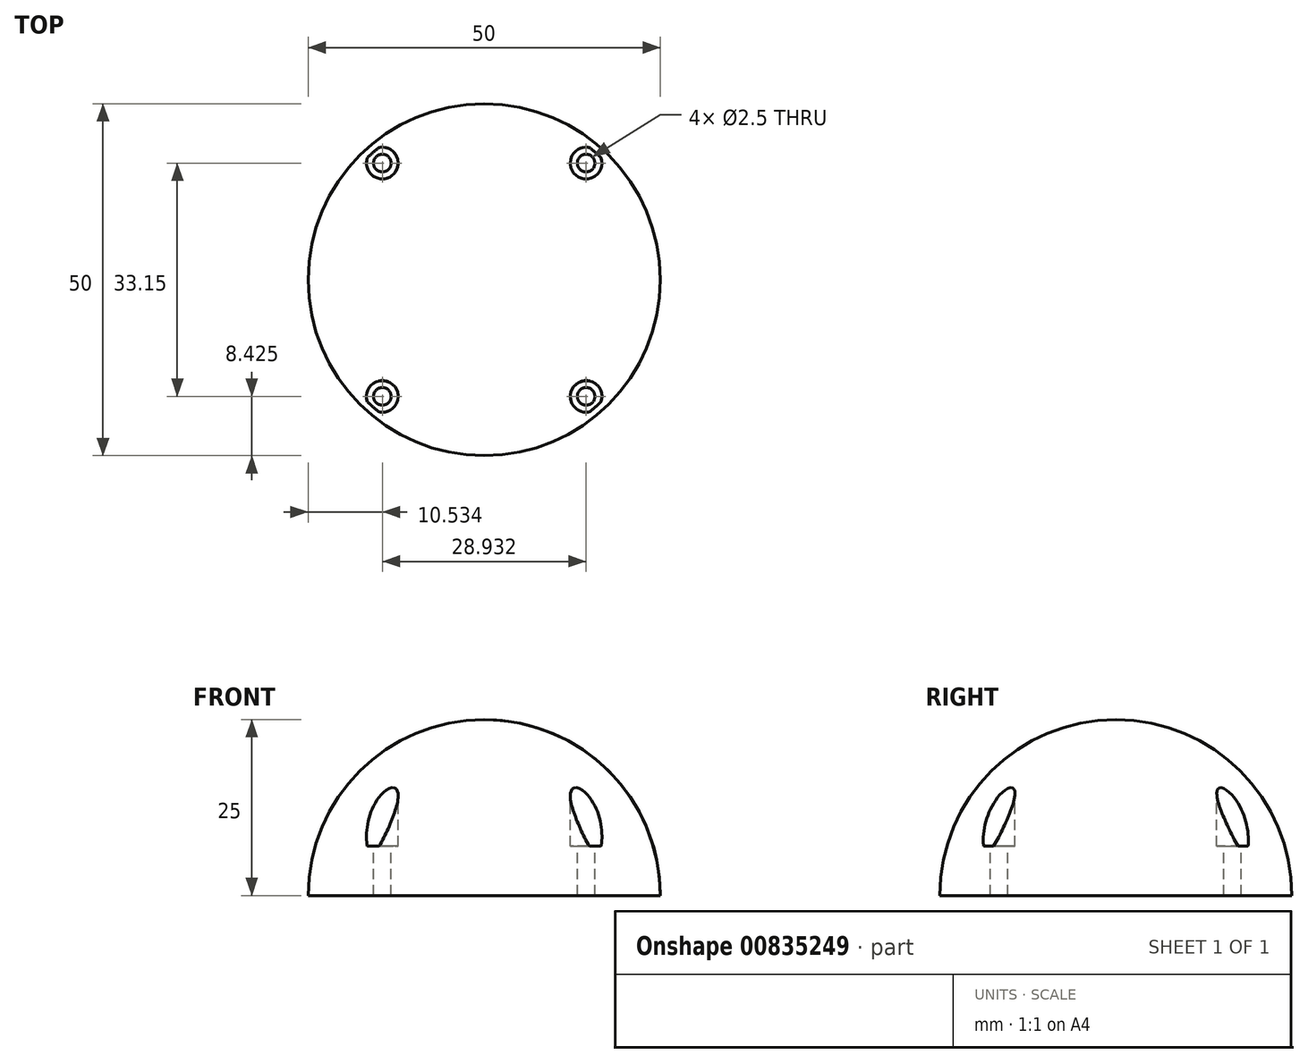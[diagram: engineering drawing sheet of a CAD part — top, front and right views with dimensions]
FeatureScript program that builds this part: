
annotation { "Feature Type Name" : "Feature", "Feature Type Description" : "" }
export const myFeature = defineFeature(function(context is Context, id is Id, definition is map)
    precondition{}
    {
        {
            var Q0;
            Q0=qCreatedBy(makeId("Top.planeOp"),FACE);
            var sketch = newSketch(context, id + "F0", { "sketchPlane" : qUnion([Q0])});
            skCircle(sketch, "E0", {"center": v(0, 0) * mm, "radius": 25 * mm});
            skSolve(sketch);
        }
        {
            var Q0;
            Q0=makeQuery(id+"F0.imprint","IMPRINT",FACE,{"disambiguationData":[TD([[makeQuery(id+"F0.imprint","IMPRINT",EDGE,{"derivedFrom":sQuery(id+"F0.wireOp",EDGE,"E0")}),1.0]])]});
            extrude(context, id + "F1", {"entities" : qUnion([Q0]), "depth" : 25 * mm, "offsetDistance" : 25 * mm});
        }
        {
            var Q0;
            Q0=makeQuery(id+"F1.opExtrude","CAP_FACE",FACE,{"disambiguationData":[OSD([sQuery(id+"F0.wireOp",EDGE,"E0")])],"isStart":false});
            var sketch = newSketch(context, id + "F2", { "sketchPlane" : qUnion([Q0])});
            skCircle(sketch, "E1", {"center": v(-14.47, -16.57) * mm, "radius": 3 * mm});
            skPoint(sketch, "E1.first.point", {"position": v(-16.44, -18.84) * mm});
            skPoint(sketch, "E1.second.point", {"position": v(-12.8, -14.08) * mm});
            skPoint(sketch, "E1.third.point", {"position": v(-15.23, -13.67) * mm});
            skCircle(sketch, "E2", {"center": v(-14.47, -16.57) * mm, "radius": 1.25 * mm});
            skCircle(sketch, "E3.MirrorC", {"center": v(-14.47, 16.57) * mm, "radius": 1.25 * mm});
            skCircle(sketch, "E4.MirrorC", {"center": v(-14.47, 16.57) * mm, "radius": 3 * mm});
            skCircle(sketch, "E5.MirrorC", {"center": v(14.47, -16.57) * mm, "radius": 1.25 * mm});
            skCircle(sketch, "E6.MirrorC", {"center": v(14.47, -16.57) * mm, "radius": 3 * mm});
            skCircle(sketch, "E7.MirrorC", {"center": v(14.47, 16.57) * mm, "radius": 3 * mm});
            skCircle(sketch, "E8.MirrorC", {"center": v(14.47, 16.57) * mm, "radius": 1.25 * mm});
            skSolve(sketch);
        }
        {
            var Q0;
            Q0=sQuery(id+"F2.wireOp",VERTEX,"E7.MirrorC.center");
            var Q1;
            Q1=sQuery(id+"F2.wireOp",VERTEX,"E5.MirrorC.center");
            var Q2;
            Q2=sQuery(id+"F2.wireOp",VERTEX,"E1.center");
            var Q3;
            Q3=sQuery(id+"F2.wireOp",VERTEX,"E3.MirrorC.center");
            var Q4;
            Q4=makeQuery(id+"F1.opExtrude","SWEPT_BODY",BODY,{"disambiguationData":[OSD([sQuery(id+"F0.wireOp",EDGE,"E0")])]});
            hole(context, id + "F3", {"style" : HoleStyle.C_BORE, "endStyle" : HoleEndStyle.THROUGH, "holeDiameter" : 2.5 * mm, "cBoreDiameter" : 4.5 * mm, "cBoreDepth" : 18 * mm, "majorDiameter" : 5 * mm, "isTappedThrough" : true, "tappedDepth" : 12 * mm, "tapClearance" : 3, "locations" : qUnion([Q0, Q1, Q2, Q3]), "scope" : qUnion([Q4])});
        }
        {
            var Q0;
            Q0=makeQuery(id+"F1.opExtrude","CAP_EDGE",EDGE,{"disambiguationData":[OSD([sQuery(id+"F0.wireOp",EDGE,"E0")])],"isStart":false});
            fillet(context, id + "F4", {"entities" : qUnion([Q0]), "radius" : 25 * mm, "tangentPropagation" : true, "allowEdgeOverflow" : false});
        }
    });
